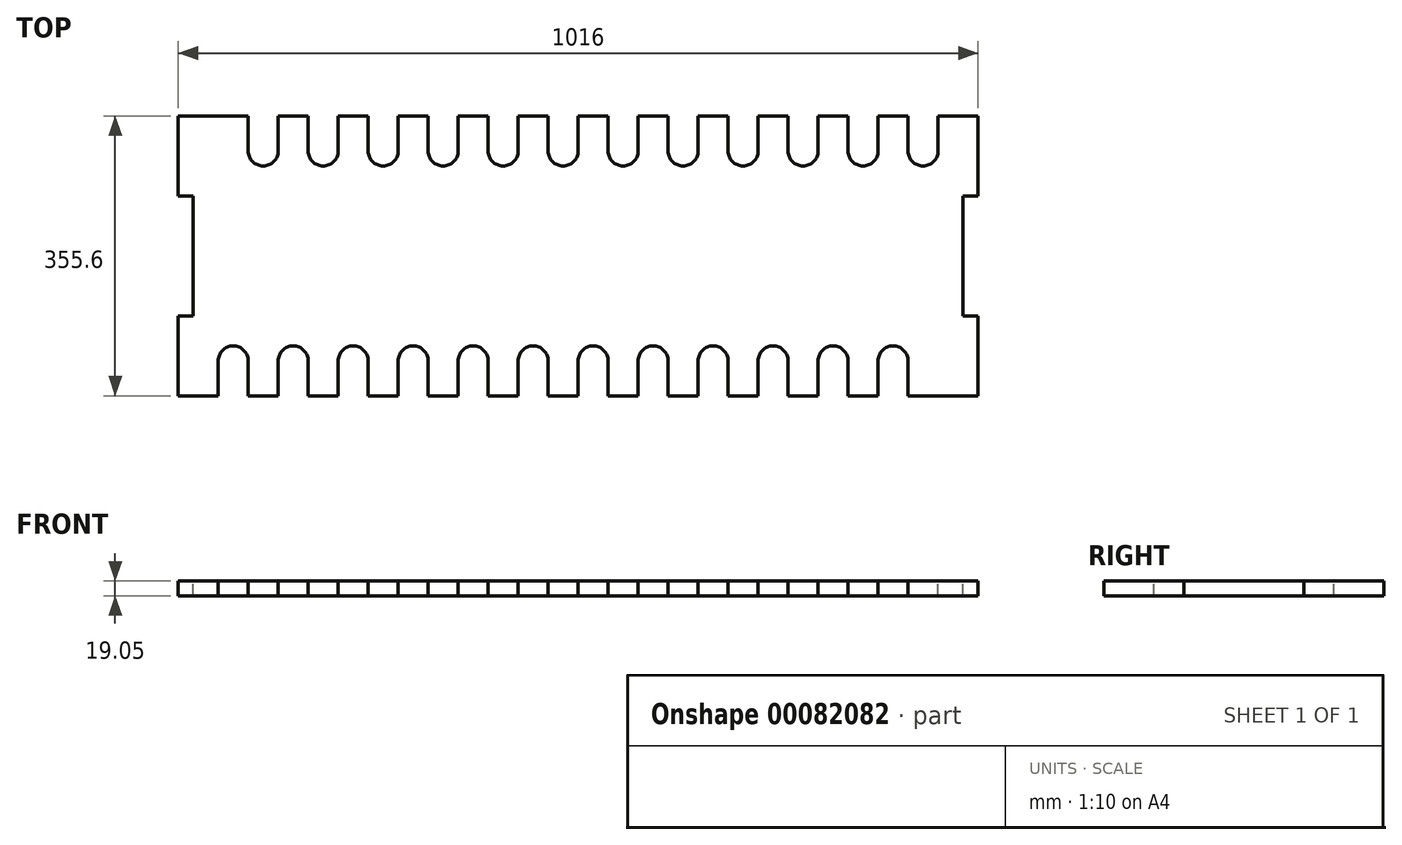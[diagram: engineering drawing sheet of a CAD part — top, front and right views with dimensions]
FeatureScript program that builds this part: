
annotation { "Feature Type Name" : "Feature", "Feature Type Description" : "" }
export const myFeature = defineFeature(function(context is Context, id is Id, definition is map)
    precondition{}
    {
        {
            var Q0;
            Q0=qCreatedBy(makeId("Top.planeOp"),FACE);
            var sketch = newSketch(context, id + "F0", { "sketchPlane" : qUnion([Q0])});
            skLineSegment(sketch, "E0.bottom", {"start": v(-530.72, 138.98) * mm, "end": v(485.28, 138.98) * mm});
            skLineSegment(sketch, "E0.top", {"start": v(-530.72, -216.62) * mm, "end": v(485.28, -216.62) * mm});
            skLineSegment(sketch, "E0.left", {"start": v(-530.72, 138.98) * mm, "end": v(-530.72, -216.62) * mm});
            skLineSegment(sketch, "E0.right", {"start": v(485.28, 138.98) * mm, "end": v(485.28, -216.62) * mm});
            skSolve(sketch);
        }
        {
            var Q0;
            Q0 = qSketchRegion(id + "F0", true);
            extrude(context, id + "F1", {"entities" : qUnion([Q0]), "depth" : 19.05 * mm});
        }
        {
            var Q0;
            Q0=makeQuery(id+"F1.opExtrude","CAP_FACE",FACE,{"disambiguationData":[OSD([sQuery(id+"F0.wireOp",EDGE,"E0.bottom"),sQuery(id+"F0.wireOp",EDGE,"E0.top"),sQuery(id+"F0.wireOp",EDGE,"E0.left"),sQuery(id+"F0.wireOp",EDGE,"E0.right")])],"isStart":false});
            var sketch = newSketch(context, id + "F2", { "sketchPlane" : qUnion([Q0])});
            skLineSegment(sketch, "E1.0", {"start": v(-441.82, 138.98) * mm, "end": v(-441.82, 94.53) * mm});
            skArc(sketch, "E2", {"start": v(-441.82, -172.17) * mm, "mid": v(-460.87, -153.12) * mm, "end": v(-479.92, -172.17) * mm});
            skLineSegment(sketch, "E3.0", {"start": v(-403.72, 138.98) * mm, "end": v(-403.72, 94.53) * mm});
            skArc(sketch, "E4", {"start": v(-441.82, 94.53) * mm, "mid": v(-422.77, 75.48) * mm, "end": v(-403.72, 94.53) * mm});
            skLineSegment(sketch, "E5", {"start": v(-441.82, -216.62) * mm, "end": v(-479.92, -216.62) * mm});
            skLineSegment(sketch, "E6", {"start": v(-441.82, 138.98) * mm, "end": v(-403.72, 138.98) * mm});
            skLineSegment(sketch, "E7.trimOffspring", {"start": v(-441.82, -172.17) * mm, "end": v(-441.82, -216.62) * mm});
            skLineSegment(sketch, "E8.trimOffspring", {"start": v(-479.92, -172.17) * mm, "end": v(-479.92, -216.62) * mm});
            skLineSegment(sketch, "E9.1.0.0", {"start": v(-365.62, 138.98) * mm, "end": v(-327.52, 138.98) * mm});
            skLineSegment(sketch, "E9.1.0.1", {"start": v(-365.62, 138.98) * mm, "end": v(-365.62, 94.53) * mm});
            skArc(sketch, "E9.1.0.2", {"start": v(-365.62, 94.53) * mm, "mid": v(-346.57, 75.48) * mm, "end": v(-327.52, 94.53) * mm});
            skLineSegment(sketch, "E9.1.0.3", {"start": v(-327.52, 138.98) * mm, "end": v(-327.52, 94.53) * mm});
            skArc(sketch, "E9.1.0.4", {"start": v(-365.62, -172.17) * mm, "mid": v(-384.67, -153.12) * mm, "end": v(-403.72, -172.17) * mm});
            skLineSegment(sketch, "E9.1.0.5", {"start": v(-403.72, -172.17) * mm, "end": v(-403.72, -216.62) * mm});
            skLineSegment(sketch, "E9.1.0.6", {"start": v(-365.62, -216.62) * mm, "end": v(-403.72, -216.62) * mm});
            skLineSegment(sketch, "E9.1.0.7", {"start": v(-365.62, -172.17) * mm, "end": v(-365.62, -216.62) * mm});
            skLineSegment(sketch, "E9.2.0.0", {"start": v(-289.42, 138.98) * mm, "end": v(-251.32, 138.98) * mm});
            skLineSegment(sketch, "E9.2.0.1", {"start": v(-289.42, 138.98) * mm, "end": v(-289.42, 94.53) * mm});
            skArc(sketch, "E9.2.0.2", {"start": v(-289.42, 94.53) * mm, "mid": v(-270.37, 75.48) * mm, "end": v(-251.32, 94.53) * mm});
            skLineSegment(sketch, "E9.2.0.3", {"start": v(-251.32, 138.98) * mm, "end": v(-251.32, 94.53) * mm});
            skArc(sketch, "E9.2.0.4", {"start": v(-289.42, -172.17) * mm, "mid": v(-308.47, -153.12) * mm, "end": v(-327.52, -172.17) * mm});
            skLineSegment(sketch, "E9.2.0.5", {"start": v(-327.52, -172.17) * mm, "end": v(-327.52, -216.62) * mm});
            skLineSegment(sketch, "E9.2.0.6", {"start": v(-289.42, -216.62) * mm, "end": v(-327.52, -216.62) * mm});
            skLineSegment(sketch, "E9.2.0.7", {"start": v(-289.42, -172.17) * mm, "end": v(-289.42, -216.62) * mm});
            skLineSegment(sketch, "E9.3.0.0", {"start": v(-213.22, 138.98) * mm, "end": v(-175.12, 138.98) * mm});
            skLineSegment(sketch, "E9.3.0.1", {"start": v(-213.22, 138.98) * mm, "end": v(-213.22, 94.53) * mm});
            skArc(sketch, "E9.3.0.2", {"start": v(-213.22, 94.53) * mm, "mid": v(-194.17, 75.48) * mm, "end": v(-175.12, 94.53) * mm});
            skLineSegment(sketch, "E9.3.0.3", {"start": v(-175.12, 138.98) * mm, "end": v(-175.12, 94.53) * mm});
            skArc(sketch, "E9.3.0.4", {"start": v(-213.22, -172.17) * mm, "mid": v(-232.27, -153.12) * mm, "end": v(-251.32, -172.17) * mm});
            skLineSegment(sketch, "E9.3.0.5", {"start": v(-251.32, -172.17) * mm, "end": v(-251.32, -216.62) * mm});
            skLineSegment(sketch, "E9.3.0.6", {"start": v(-213.22, -216.62) * mm, "end": v(-251.32, -216.62) * mm});
            skLineSegment(sketch, "E9.3.0.7", {"start": v(-213.22, -172.17) * mm, "end": v(-213.22, -216.62) * mm});
            skLineSegment(sketch, "E9.4.0.0", {"start": v(-137.02, 138.98) * mm, "end": v(-98.92, 138.98) * mm});
            skLineSegment(sketch, "E9.4.0.1", {"start": v(-137.02, 138.98) * mm, "end": v(-137.02, 94.53) * mm});
            skArc(sketch, "E9.4.0.2", {"start": v(-137.02, 94.53) * mm, "mid": v(-117.97, 75.48) * mm, "end": v(-98.92, 94.53) * mm});
            skLineSegment(sketch, "E9.4.0.3", {"start": v(-98.92, 138.98) * mm, "end": v(-98.92, 94.53) * mm});
            skArc(sketch, "E9.4.0.4", {"start": v(-137.02, -172.17) * mm, "mid": v(-156.07, -153.12) * mm, "end": v(-175.12, -172.17) * mm});
            skLineSegment(sketch, "E9.4.0.5", {"start": v(-175.12, -172.17) * mm, "end": v(-175.12, -216.62) * mm});
            skLineSegment(sketch, "E9.4.0.6", {"start": v(-137.02, -216.62) * mm, "end": v(-175.12, -216.62) * mm});
            skLineSegment(sketch, "E9.4.0.7", {"start": v(-137.02, -172.17) * mm, "end": v(-137.02, -216.62) * mm});
            skLineSegment(sketch, "E9.5.0.0", {"start": v(-60.82, 138.98) * mm, "end": v(-22.72, 138.98) * mm});
            skLineSegment(sketch, "E9.5.0.1", {"start": v(-60.82, 138.98) * mm, "end": v(-60.82, 94.53) * mm});
            skArc(sketch, "E9.5.0.2", {"start": v(-60.82, 94.53) * mm, "mid": v(-41.77, 75.48) * mm, "end": v(-22.72, 94.53) * mm});
            skLineSegment(sketch, "E9.5.0.3", {"start": v(-22.72, 138.98) * mm, "end": v(-22.72, 94.53) * mm});
            skArc(sketch, "E9.5.0.4", {"start": v(-60.82, -172.17) * mm, "mid": v(-79.87, -153.12) * mm, "end": v(-98.92, -172.17) * mm});
            skLineSegment(sketch, "E9.5.0.5", {"start": v(-98.92, -172.17) * mm, "end": v(-98.92, -216.62) * mm});
            skLineSegment(sketch, "E9.5.0.6", {"start": v(-60.82, -216.62) * mm, "end": v(-98.92, -216.62) * mm});
            skLineSegment(sketch, "E9.5.0.7", {"start": v(-60.82, -172.17) * mm, "end": v(-60.82, -216.62) * mm});
            skLineSegment(sketch, "E9.6.0.0", {"start": v(15.38, 138.98) * mm, "end": v(53.48, 138.98) * mm});
            skLineSegment(sketch, "E9.6.0.1", {"start": v(15.38, 138.98) * mm, "end": v(15.38, 94.53) * mm});
            skArc(sketch, "E9.6.0.2", {"start": v(15.38, 94.53) * mm, "mid": v(34.43, 75.48) * mm, "end": v(53.48, 94.53) * mm});
            skLineSegment(sketch, "E9.6.0.3", {"start": v(53.48, 138.98) * mm, "end": v(53.48, 94.53) * mm});
            skArc(sketch, "E9.6.0.4", {"start": v(15.38, -172.17) * mm, "mid": v(-3.67, -153.12) * mm, "end": v(-22.72, -172.17) * mm});
            skLineSegment(sketch, "E9.6.0.5", {"start": v(-22.72, -172.17) * mm, "end": v(-22.72, -216.62) * mm});
            skLineSegment(sketch, "E9.6.0.6", {"start": v(15.38, -216.62) * mm, "end": v(-22.72, -216.62) * mm});
            skLineSegment(sketch, "E9.6.0.7", {"start": v(15.38, -172.17) * mm, "end": v(15.38, -216.62) * mm});
            skLineSegment(sketch, "E9.7.0.0", {"start": v(91.58, 138.98) * mm, "end": v(129.68, 138.98) * mm});
            skLineSegment(sketch, "E9.7.0.1", {"start": v(91.58, 138.98) * mm, "end": v(91.58, 94.53) * mm});
            skArc(sketch, "E9.7.0.2", {"start": v(91.58, 94.53) * mm, "mid": v(110.63, 75.48) * mm, "end": v(129.68, 94.53) * mm});
            skLineSegment(sketch, "E9.7.0.3", {"start": v(129.68, 138.98) * mm, "end": v(129.68, 94.53) * mm});
            skArc(sketch, "E9.7.0.4", {"start": v(91.58, -172.17) * mm, "mid": v(72.53, -153.12) * mm, "end": v(53.48, -172.17) * mm});
            skLineSegment(sketch, "E9.7.0.5", {"start": v(53.48, -172.17) * mm, "end": v(53.48, -216.62) * mm});
            skLineSegment(sketch, "E9.7.0.6", {"start": v(91.58, -216.62) * mm, "end": v(53.48, -216.62) * mm});
            skLineSegment(sketch, "E9.7.0.7", {"start": v(91.58, -172.17) * mm, "end": v(91.58, -216.62) * mm});
            skLineSegment(sketch, "E9.8.0.0", {"start": v(167.78, 138.98) * mm, "end": v(205.88, 138.98) * mm});
            skLineSegment(sketch, "E9.8.0.1", {"start": v(167.78, 138.98) * mm, "end": v(167.78, 94.53) * mm});
            skArc(sketch, "E9.8.0.2", {"start": v(167.78, 94.53) * mm, "mid": v(186.83, 75.48) * mm, "end": v(205.88, 94.53) * mm});
            skLineSegment(sketch, "E9.8.0.3", {"start": v(205.88, 138.98) * mm, "end": v(205.88, 94.53) * mm});
            skArc(sketch, "E9.8.0.4", {"start": v(167.78, -172.17) * mm, "mid": v(148.73, -153.12) * mm, "end": v(129.68, -172.17) * mm});
            skLineSegment(sketch, "E9.8.0.5", {"start": v(129.68, -172.17) * mm, "end": v(129.68, -216.62) * mm});
            skLineSegment(sketch, "E9.8.0.6", {"start": v(167.78, -216.62) * mm, "end": v(129.68, -216.62) * mm});
            skLineSegment(sketch, "E9.8.0.7", {"start": v(167.78, -172.17) * mm, "end": v(167.78, -216.62) * mm});
            skLineSegment(sketch, "E9.direction1", {"start": v(-441.82, 138.98) * mm, "end": v(-365.62, 138.98) * mm, "construction": true});
            skLineSegment(sketch, "E10.1.0.0", {"start": v(282.08, 138.98) * mm, "end": v(282.08, 94.53) * mm});
            skArc(sketch, "E10.1.0.1", {"start": v(243.98, 94.53) * mm, "mid": v(263.03, 75.48) * mm, "end": v(282.08, 94.53) * mm});
            skLineSegment(sketch, "E10.1.0.2", {"start": v(243.98, 138.98) * mm, "end": v(243.98, 94.53) * mm});
            skLineSegment(sketch, "E10.1.0.3", {"start": v(243.98, 138.98) * mm, "end": v(282.08, 138.98) * mm});
            skLineSegment(sketch, "E10.1.0.4", {"start": v(243.98, -172.17) * mm, "end": v(243.98, -216.62) * mm});
            skLineSegment(sketch, "E10.1.0.5", {"start": v(243.98, -216.62) * mm, "end": v(205.88, -216.62) * mm});
            skLineSegment(sketch, "E10.1.0.6", {"start": v(205.88, -172.17) * mm, "end": v(205.88, -216.62) * mm});
            skArc(sketch, "E10.1.0.7", {"start": v(243.98, -172.17) * mm, "mid": v(224.93, -153.12) * mm, "end": v(205.88, -172.17) * mm});
            skLineSegment(sketch, "E10.2.0.0", {"start": v(358.28, 138.98) * mm, "end": v(358.28, 94.53) * mm});
            skArc(sketch, "E10.2.0.1", {"start": v(320.18, 94.53) * mm, "mid": v(339.23, 75.48) * mm, "end": v(358.28, 94.53) * mm});
            skLineSegment(sketch, "E10.2.0.2", {"start": v(320.18, 138.98) * mm, "end": v(320.18, 94.53) * mm});
            skLineSegment(sketch, "E10.2.0.3", {"start": v(320.18, 138.98) * mm, "end": v(358.28, 138.98) * mm});
            skLineSegment(sketch, "E10.2.0.4", {"start": v(320.18, -172.17) * mm, "end": v(320.18, -216.62) * mm});
            skLineSegment(sketch, "E10.2.0.5", {"start": v(320.18, -216.62) * mm, "end": v(282.08, -216.62) * mm});
            skLineSegment(sketch, "E10.2.0.6", {"start": v(282.08, -172.17) * mm, "end": v(282.08, -216.62) * mm});
            skArc(sketch, "E10.2.0.7", {"start": v(320.18, -172.17) * mm, "mid": v(301.13, -153.12) * mm, "end": v(282.08, -172.17) * mm});
            skLineSegment(sketch, "E10.3.0.0", {"start": v(434.48, 138.98) * mm, "end": v(434.48, 94.53) * mm});
            skArc(sketch, "E10.3.0.1", {"start": v(396.38, 94.53) * mm, "mid": v(415.43, 75.48) * mm, "end": v(434.48, 94.53) * mm});
            skLineSegment(sketch, "E10.3.0.2", {"start": v(396.38, 138.98) * mm, "end": v(396.38, 94.53) * mm});
            skLineSegment(sketch, "E10.3.0.3", {"start": v(396.38, 138.98) * mm, "end": v(434.48, 138.98) * mm});
            skLineSegment(sketch, "E10.3.0.4", {"start": v(396.38, -172.17) * mm, "end": v(396.38, -216.62) * mm});
            skLineSegment(sketch, "E10.3.0.5", {"start": v(396.38, -216.62) * mm, "end": v(358.28, -216.62) * mm});
            skLineSegment(sketch, "E10.3.0.6", {"start": v(358.28, -172.17) * mm, "end": v(358.28, -216.62) * mm});
            skArc(sketch, "E10.3.0.7", {"start": v(396.38, -172.17) * mm, "mid": v(377.33, -153.12) * mm, "end": v(358.28, -172.17) * mm});
            skLineSegment(sketch, "E10.direction1", {"start": v(205.88, 94.53) * mm, "end": v(282.08, 94.53) * mm, "construction": true});
            skSolve(sketch);
        }
        {
            var Q0;
            Q0 = qSketchRegion(id + "F2", true);
            extrude(context, id + "F3", {"entities" : qUnion([Q0]), "operationType" : NewBodyOperationType.REMOVE, "endBound" : BoundingType.THROUGH_ALL, "oppositeDirection" : true, "depth" : 25.4 * mm});
        }
        {
            var Q0;
            Q0=makeQuery(id+"F1.opExtrude","CAP_FACE",FACE,{"disambiguationData":[OSD([sQuery(id+"F0.wireOp",EDGE,"E0.bottom"),sQuery(id+"F0.wireOp",EDGE,"E0.top"),sQuery(id+"F0.wireOp",EDGE,"E0.left"),sQuery(id+"F0.wireOp",EDGE,"E0.right")])],"isStart":false});
            var sketch = newSketch(context, id + "F4", { "sketchPlane" : qUnion([Q0])});
            skLineSegment(sketch, "E11", {"start": v(-518.02, -38.82) * mm, "end": v(-518.02, 37.38) * mm});
            skLineSegment(sketch, "E12", {"start": v(-518.02, 37.38) * mm, "end": v(-530.72, 37.38) * mm});
            skLineSegment(sketch, "E13", {"start": v(-530.72, 37.38) * mm, "end": v(-530.72, -38.82) * mm});
            skLineSegment(sketch, "E14", {"start": v(-530.72, -216.62) * mm, "end": v(485.28, -216.62) * mm});
            skLineSegment(sketch, "E15", {"start": v(-22.72, -216.62) * mm, "end": v(-22.72, -46.4) * mm});
            skLineSegment(sketch, "E16.MirrorCS", {"start": v(-518.02, -115.02) * mm, "end": v(-530.72, -115.02) * mm});
            skLineSegment(sketch, "E17.MirrorCS", {"start": v(-518.02, -38.82) * mm, "end": v(-518.02, -115.02) * mm});
            skLineSegment(sketch, "E18.MirrorCS", {"start": v(-530.72, -115.02) * mm, "end": v(-530.72, -38.82) * mm});
            skLineSegment(sketch, "E19.MirrorCS", {"start": v(472.58, 37.38) * mm, "end": v(485.28, 37.38) * mm});
            skLineSegment(sketch, "E20.MirrorCS", {"start": v(472.58, -115.02) * mm, "end": v(485.28, -115.02) * mm});
            skLineSegment(sketch, "E21.MirrorCS", {"start": v(472.58, -38.82) * mm, "end": v(472.58, 37.38) * mm});
            skLineSegment(sketch, "E22.MirrorCS", {"start": v(485.28, 37.38) * mm, "end": v(485.28, -38.82) * mm});
            skLineSegment(sketch, "E23.MirrorCS", {"start": v(472.58, -38.82) * mm, "end": v(472.58, -115.02) * mm});
            skLineSegment(sketch, "E24.MirrorCS", {"start": v(485.28, -115.02) * mm, "end": v(485.28, -38.82) * mm});
            skSolve(sketch);
        }
        {
            var Q0;
            Q0 = qSketchRegion(id + "F4", true);
            extrude(context, id + "F5", {"entities" : qUnion([Q0]), "operationType" : NewBodyOperationType.REMOVE, "endBound" : BoundingType.THROUGH_ALL, "oppositeDirection" : true, "depth" : 25.4 * mm});
        }
        {
            var Q0;
            Q0=makeQuery(id+"F1.opExtrude","CAP_FACE",FACE,{"disambiguationData":[OSD([sQuery(id+"F0.wireOp",EDGE,"E0.bottom"),sQuery(id+"F0.wireOp",EDGE,"E0.top"),sQuery(id+"F0.wireOp",EDGE,"E0.left"),sQuery(id+"F0.wireOp",EDGE,"E0.right")])],"isStart":false});
            var sketch = newSketch(context, id + "F6", { "sketchPlane" : qUnion([Q0])});
            skLineSegment(sketch, "E25.bottom", {"start": v(-518.02, 37.38) * mm, "end": v(-511.67, 37.38) * mm});
            skLineSegment(sketch, "E25.top", {"start": v(-518.02, -115.02) * mm, "end": v(-511.67, -115.02) * mm});
            skLineSegment(sketch, "E25.left", {"start": v(-518.02, 37.38) * mm, "end": v(-518.02, -115.02) * mm});
            skLineSegment(sketch, "E25.right", {"start": v(-511.67, 37.38) * mm, "end": v(-511.67, -115.02) * mm});
            skLineSegment(sketch, "E26.bottom", {"start": v(472.58, 37.38) * mm, "end": v(466.23, 37.38) * mm});
            skLineSegment(sketch, "E26.top", {"start": v(472.58, -115.02) * mm, "end": v(466.23, -115.02) * mm});
            skLineSegment(sketch, "E26.left", {"start": v(472.58, 37.38) * mm, "end": v(472.58, -115.02) * mm});
            skLineSegment(sketch, "E26.right", {"start": v(466.23, 37.38) * mm, "end": v(466.23, -115.02) * mm});
            skSolve(sketch);
        }
        {
            var Q0;
            Q0 = qSketchRegion(id + "F6", true);
            extrude(context, id + "F7", {"entities" : qUnion([Q0]), "operationType" : NewBodyOperationType.REMOVE, "endBound" : BoundingType.THROUGH_ALL, "oppositeDirection" : true, "depth" : 25.4 * mm});
        }
    });
